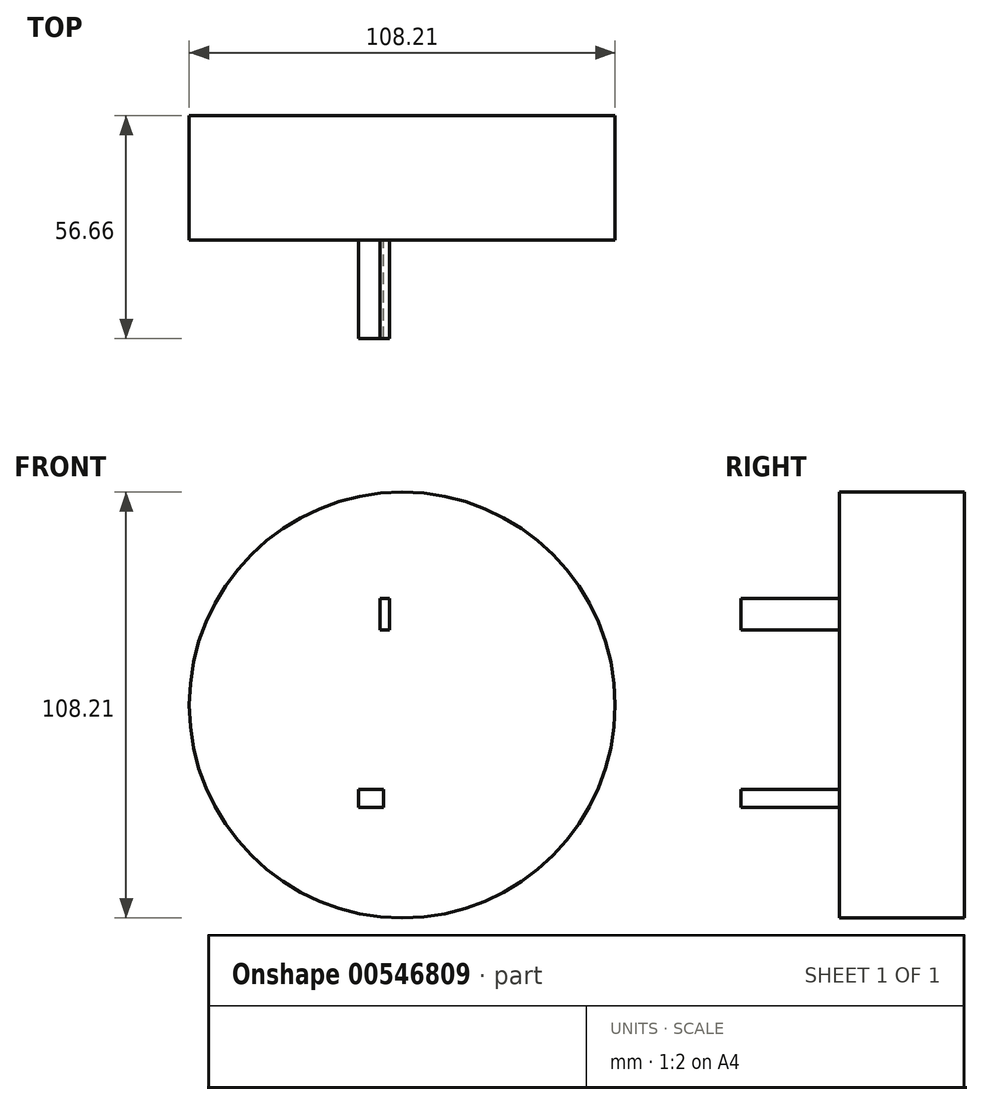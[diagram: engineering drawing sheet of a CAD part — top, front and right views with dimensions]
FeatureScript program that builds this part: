
annotation { "Feature Type Name" : "Feature", "Feature Type Description" : "" }
export const myFeature = defineFeature(function(context is Context, id is Id, definition is map)
    precondition{}
    {
        {
            var Q0;
            Q0=qCreatedBy(makeId("Front.planeOp"),FACE);
            var sketch = newSketch(context, id + "F0", { "sketchPlane" : qUnion([Q0])});
            skLineSegment(sketch, "E0.bottom", {"start": v(55.65, 27.8) * mm, "end": v(62.07, 27.8) * mm});
            skLineSegment(sketch, "E0.top", {"start": v(55.65, 23.24) * mm, "end": v(62.07, 23.24) * mm});
            skLineSegment(sketch, "E0.left", {"start": v(55.65, 27.8) * mm, "end": v(55.65, 23.24) * mm});
            skLineSegment(sketch, "E0.right", {"start": v(62.07, 27.8) * mm, "end": v(62.07, 23.24) * mm});
            skLineSegment(sketch, "E1.bottom", {"start": v(61.07, 68.29) * mm, "end": v(63.47, 68.29) * mm});
            skLineSegment(sketch, "E1.top", {"start": v(61.07, 76.2) * mm, "end": v(63.47, 76.2) * mm});
            skLineSegment(sketch, "E1.left", {"start": v(61.07, 68.29) * mm, "end": v(61.07, 76.2) * mm});
            skLineSegment(sketch, "E1.right", {"start": v(63.47, 68.29) * mm, "end": v(63.47, 76.2) * mm});
            skSolve(sketch);
        }
        {
            var Q0;
            Q0 = qSketchRegion(id + "F0", true);
            extrude(context, id + "F1", {"entities" : qUnion([Q0]), "depth" : 25 * mm, "offsetDistance" : 25 * mm});
        }
        {
            var Q0;
            Q0=qCreatedBy(makeId("Front.planeOp"),FACE);
            var sketch = newSketch(context, id + "F2", { "sketchPlane" : qUnion([Q0])});
            skCircle(sketch, "E2", {"center": v(66.76, 49.2) * mm, "radius": 54.1 * mm});
            skSolve(sketch);
        }
        {
            var Q0;
            Q0 = qSketchRegion(id + "F2", true);
            extrude(context, id + "F3", {"entities" : qUnion([Q0]), "oppositeDirection" : true, "depth" : 31.66 * mm, "offsetDistance" : 25 * mm});
        }
    });
